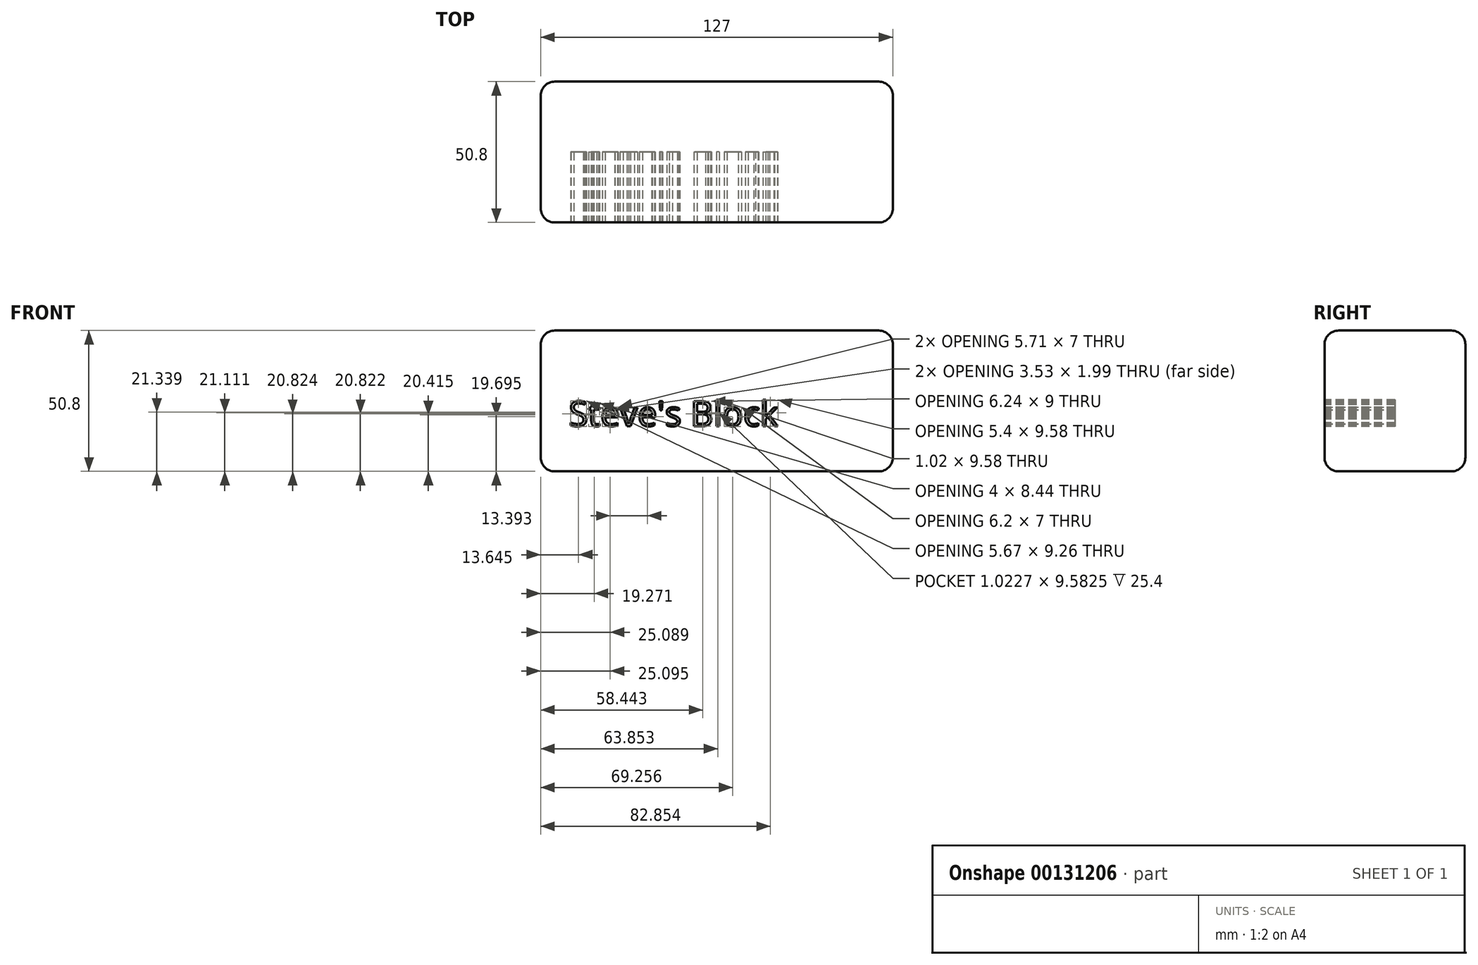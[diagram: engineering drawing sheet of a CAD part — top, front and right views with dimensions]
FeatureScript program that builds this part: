
annotation { "Feature Type Name" : "Feature", "Feature Type Description" : "" }
export const myFeature = defineFeature(function(context is Context, id is Id, definition is map)
    precondition{}
    {
        {
            var Q0;
            Q0=qCreatedBy(makeId("Top.planeOp"),FACE);
            var sketch = newSketch(context, id + "F0", { "sketchPlane" : qUnion([Q0])});
            skLineSegment(sketch, "E0.bottom", {"start": v(-58.08, 31.5) * mm, "end": v(68.92, 31.5) * mm});
            skLineSegment(sketch, "E0.top", {"start": v(-58.08, -19.3) * mm, "end": v(68.92, -19.3) * mm});
            skLineSegment(sketch, "E0.left", {"start": v(-58.08, 31.5) * mm, "end": v(-58.08, -19.3) * mm});
            skLineSegment(sketch, "E0.right", {"start": v(68.92, 31.5) * mm, "end": v(68.92, -19.3) * mm});
            skSolve(sketch);
        }
        {
            var Q0;
            Q0 = qSketchRegion(id + "F0", true);
            extrude(context, id + "F1", {"entities" : qUnion([Q0]), "depth" : 50.8 * mm});
        }
        {
            var Q0;
            Q0=makeQuery(id+"F1.opExtrude","CAP_FACE",FACE,{"disambiguationData":[OSD([sQuery(id+"F0.wireOp",EDGE,"E0.bottom"),sQuery(id+"F0.wireOp",EDGE,"E0.top"),sQuery(id+"F0.wireOp",EDGE,"E0.left"),sQuery(id+"F0.wireOp",EDGE,"E0.right")])],"isStart":false});
            var Q1;
            Q1=makeQuery(id+"F1.opExtrude","SWEPT_FACE",FACE,{"disambiguationData":[OSD([sQuery(id+"F0.wireOp",EDGE,"E0.right")])]});
            var Q2;
            Q2=makeQuery(id+"F1.opExtrude","SWEPT_FACE",FACE,{"disambiguationData":[OSD([sQuery(id+"F0.wireOp",EDGE,"E0.left")])]});
            var Q3;
            Q3=makeQuery(id+"F1.opExtrude","CAP_FACE",FACE,{"disambiguationData":[OSD([sQuery(id+"F0.wireOp",EDGE,"E0.bottom"),sQuery(id+"F0.wireOp",EDGE,"E0.top"),sQuery(id+"F0.wireOp",EDGE,"E0.left"),sQuery(id+"F0.wireOp",EDGE,"E0.right")])],"isStart":true});
            fillet(context, id + "F2", {"entities" : qUnion([Q0, Q1, Q2, Q3]), "radius" : 5.08 * mm, "tangentPropagation" : true, "allowEdgeOverflow" : false});
        }
        {
            var Q0;
            Q0=makeQuery(id+"F1.opExtrude","SWEPT_FACE",FACE,{"disambiguationData":[OSD([sQuery(id+"F0.wireOp",EDGE,"E0.top")])]});
            var sketch = newSketch(context, id + "F3", { "sketchPlane" : qUnion([Q0])});
            skText(sketch, "E1", { "text": "Steve\'s Block\n", "fontName": "OpenSans-Regular.ttf"});
            skPoint(sketch, "E1.firstSnap0", {"position": v(-53, 25.4) * mm});
            const initialGuessF3  = {"E1": [-0.04792, 0.01632, 1, 0, 0.00908]};
            skSetInitialGuess(sketch, initialGuessF3);
            skSolve(sketch);
        }
        {
            var Q0;
            Q0 = qSketchRegion(id + "F3", true);
            extrude(context, id + "F4", {"entities" : qUnion([Q0]), "operationType" : NewBodyOperationType.REMOVE, "oppositeDirection" : true, "depth" : 25.4 * mm});
        }
    });
